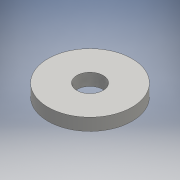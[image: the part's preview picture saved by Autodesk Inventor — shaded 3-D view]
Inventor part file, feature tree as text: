
AUTODESK INVENTOR PART (.ipt)
format: ipt  version: 2016 (Build 200138000, 138)  size: 93,184 bytes
history: native  units: mm
features: other x1, extrude x1, sketch x1
ambient origin geometry x8: Origin, YZ Plane, XZ Plane, XY Plane, X Axis, Y Axis, Z Axis, Center Point
bodies: Body1 (feature_tree)
feature tree (3):
  other  "ソリッド1"
  extrude  "押し出し1"  Depth=15.0mm
  sketch  "スケッチ1"
